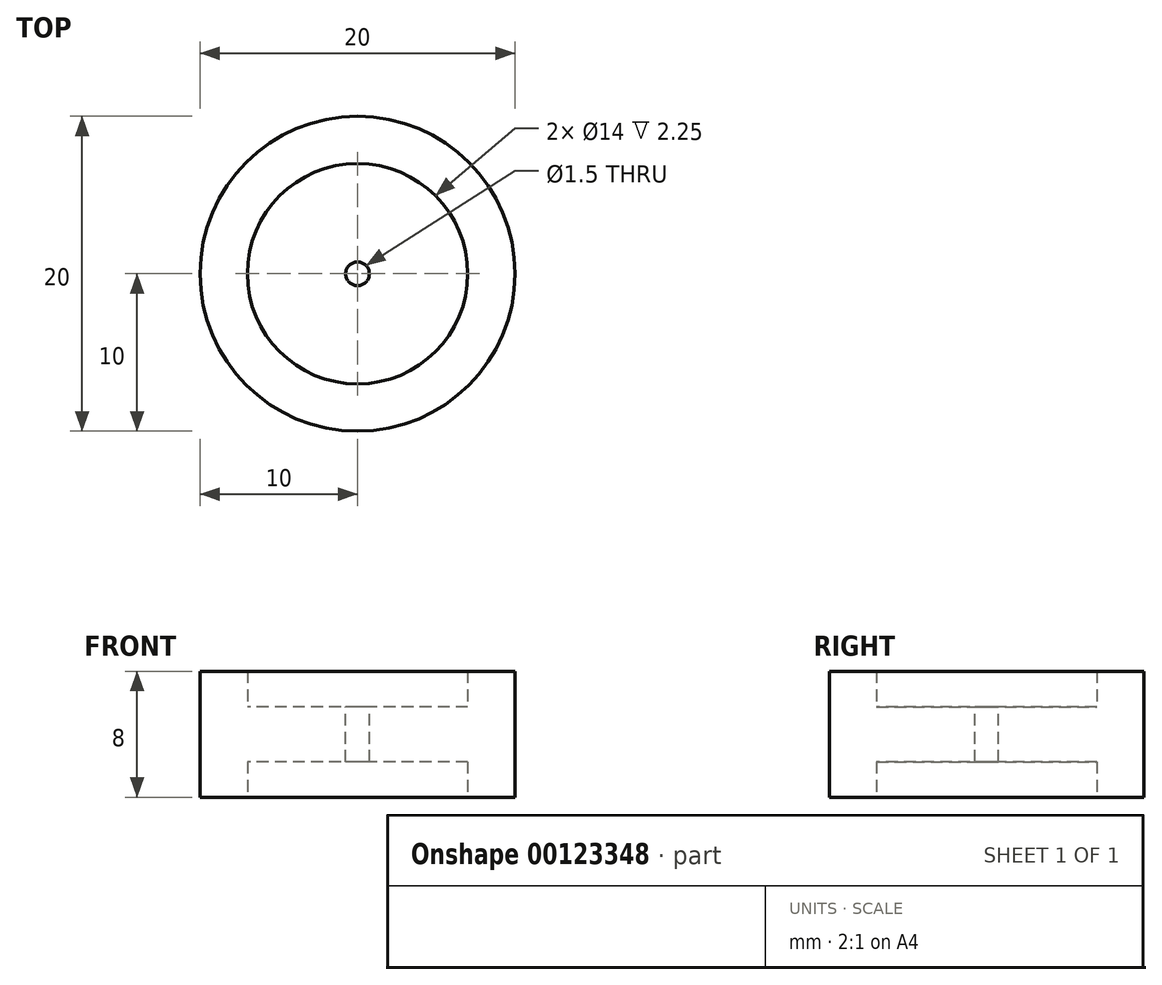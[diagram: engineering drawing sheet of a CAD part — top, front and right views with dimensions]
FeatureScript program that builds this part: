
annotation { "Feature Type Name" : "Feature", "Feature Type Description" : "" }
export const myFeature = defineFeature(function(context is Context, id is Id, definition is map)
    precondition{}
    {
        {
            var Q0;
            Q0=qCreatedBy(makeId("Top.planeOp"),FACE);
            var sketch = newSketch(context, id + "F0", { "sketchPlane" : qUnion([Q0])});
            skCircle(sketch, "E0", {"center": v(0, 0) * mm, "radius": 10 * mm});
            skSolve(sketch);
        }
        {
            var Q0;
            Q0=makeQuery(id+"F0.imprint","IMPRINT",FACE,{"disambiguationData":[TD([[makeQuery(id+"F0.imprint","IMPRINT",EDGE,{"derivedFrom":sQuery(id+"F0.wireOp",EDGE,"E0")}),1.0]])]});
            extrude(context, id + "F1", {"entities" : qUnion([Q0]), "endBound" : BoundingType.SYMMETRIC, "depth" : 3.5 * mm});
        }
        {
            var Q0;
            Q0=makeQuery(id+"F1.opExtrude","CAP_FACE",FACE,{"disambiguationData":[OSD([sQuery(id+"F0.wireOp",EDGE,"E0")])],"isStart":false});
            var sketch = newSketch(context, id + "F2", { "sketchPlane" : qUnion([Q0])});
            skCircle(sketch, "E1", {"center": v(0, 0) * mm, "radius": 0.75 * mm});
            skSolve(sketch);
        }
        {
            var Q0;
            Q0=makeQuery(id+"F2.imprint","IMPRINT",FACE,{"disambiguationData":[TD([[makeQuery(id+"F2.imprint","IMPRINT",EDGE,{"derivedFrom":sQuery(id+"F2.wireOp",EDGE,"E1")}),1.0]])]});
            extrude(context, id + "F3", {"entities" : qUnion([Q0]), "operationType" : NewBodyOperationType.REMOVE, "endBound" : BoundingType.SYMMETRIC, "oppositeDirection" : true, "depth" : 20 * mm});
        }
        {
            var Q0;
            Q0=qCreatedBy(makeId("Top.planeOp"),FACE);
            var sketch = newSketch(context, id + "F4", { "sketchPlane" : qUnion([Q0])});
            skCircle(sketch, "E2", {"center": v(0, 0) * mm, "radius": 7 * mm});
            skCircle(sketch, "E3", {"center": v(0, 0) * mm, "radius": 10 * mm});
            skSolve(sketch);
        }
        {
            var Q0;
            Q0=makeQuery(id+"F4.imprint","IMPRINT",FACE,{"disambiguationData":[TD([[makeQuery(id+"F4.imprint","IMPRINT",EDGE,{"derivedFrom":sQuery(id+"F4.wireOp",EDGE,"E2")}),-1.0]])]});
            extrude(context, id + "F5", {"entities" : qUnion([Q0]), "operationType" : NewBodyOperationType.ADD, "endBound" : BoundingType.SYMMETRIC, "depth" : 8 * mm});
        }
    });
